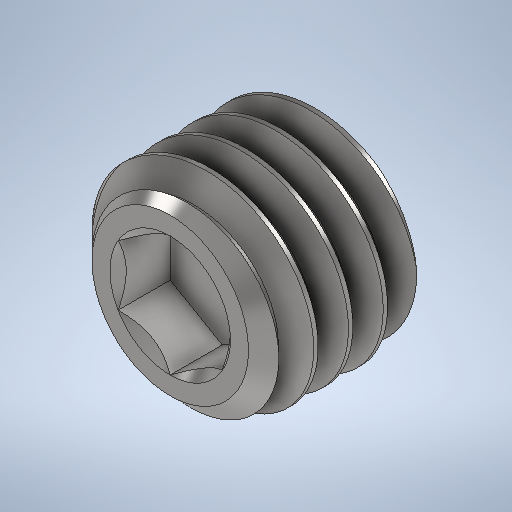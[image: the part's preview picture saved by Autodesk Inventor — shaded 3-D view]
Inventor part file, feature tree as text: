
AUTODESK INVENTOR PART (.ipt)
format: ipt  version: 2025 (Build 290162000, 162)  size: 492,544 bytes
history: native  units: mm
features: sketch x2, sweep x1, fillet x1, other x1
ambient origin geometry x8: Origin, YZ Plane, XZ Plane, XY Plane, X Axis, Y Axis, Z Axis, Center Point
bodies: Solid1 (feature_tree)
feature tree (5):
  sweep  "Sweep1"
  fillet  "Fillet1"  [1 undecoded]
  sketch  "Sketch1"  dims[d0=1.25mm d1=3.0mm d2=0.0mm d3=0.0mm d4=0.2mm]
  sketch  "3D Sketch1"
  other  "Cut-Sweep1"
note: 1 required parameter value undecoded (feature->parameter linkage not recoverable at this tier; creation-order binding heuristic only, values carry confidence <= 0.55)
